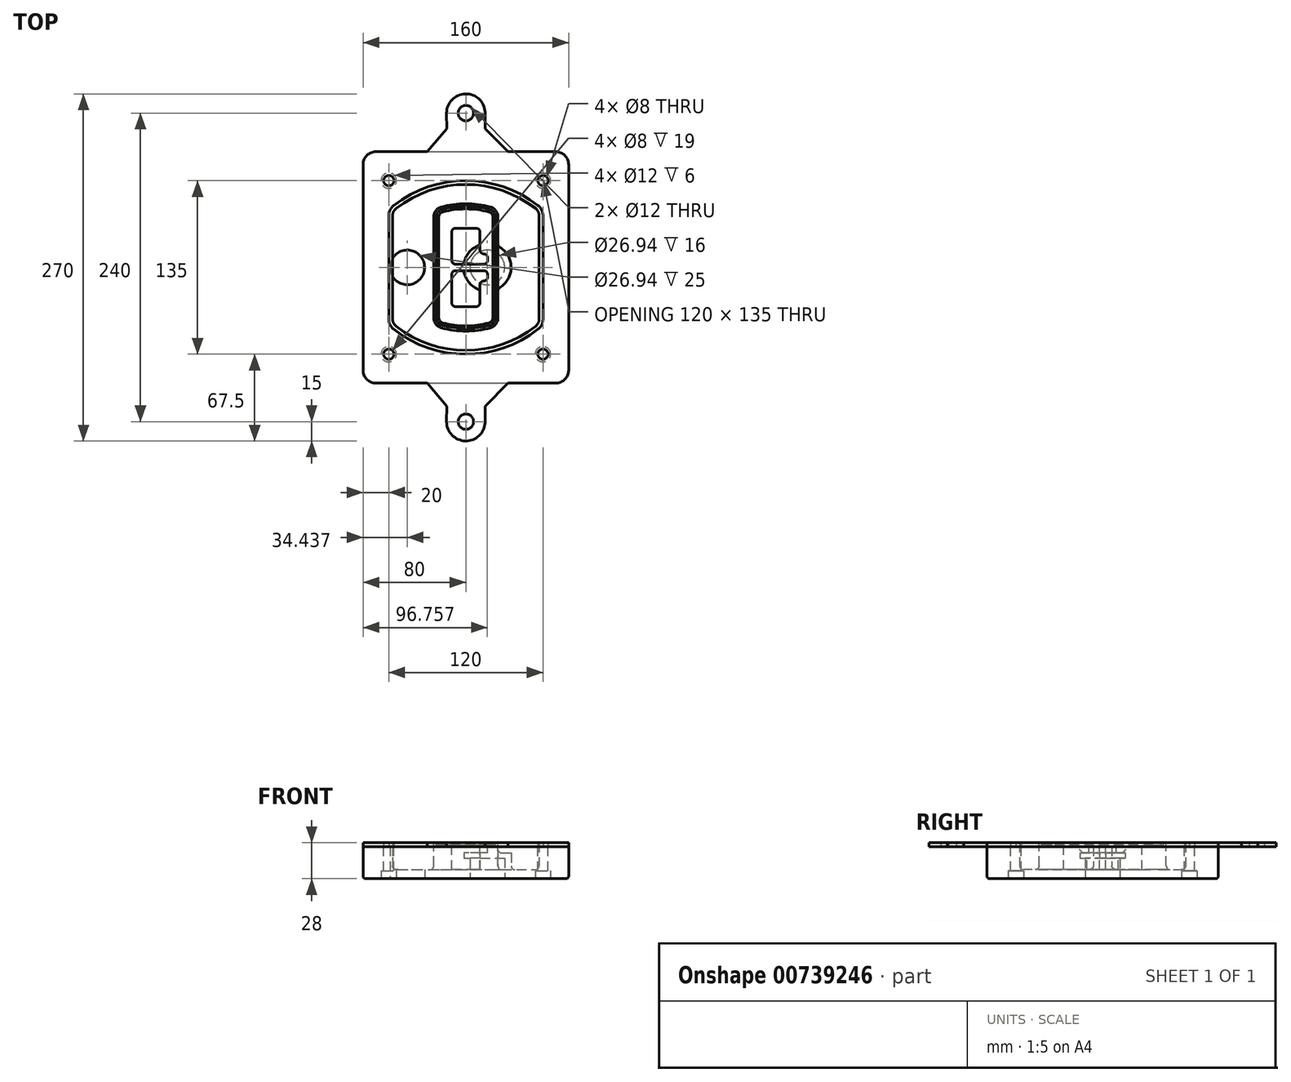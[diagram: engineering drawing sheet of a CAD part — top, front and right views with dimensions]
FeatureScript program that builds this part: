
annotation { "Feature Type Name" : "Feature", "Feature Type Description" : "" }
export const myFeature = defineFeature(function(context is Context, id is Id, definition is map)
    precondition{}
    {
        {
            var Q0;
            Q0=qCreatedBy(makeId("Top.planeOp"),FACE);
            var sketch = newSketch(context, id + "F0", { "sketchPlane" : qUnion([Q0])});
            skPoint(sketch, "E0.rect.middle", {"position": v(0, 0) * mm});
            skLineSegment(sketch, "E1.bottom", {"start": v(-70, -90) * mm, "end": v(70, -90) * mm});
            skLineSegment(sketch, "E1.top", {"start": v(-70, 90) * mm, "end": v(70, 90) * mm});
            skLineSegment(sketch, "E1.left", {"start": v(-80, -80) * mm, "end": v(-80, 80) * mm});
            skLineSegment(sketch, "E1.right", {"start": v(80, -80) * mm, "end": v(80, 80) * mm});
            skLineSegment(sketch, "E2", {"start": v(-80, 90) * mm, "end": v(80, -90) * mm, "construction": true});
            skLineSegment(sketch, "E3", {"start": v(80, 90) * mm, "end": v(-80, -90) * mm, "construction": true});
            skCircle(sketch, "E4", {"center": v(-60, 67.5) * mm, "radius": 4 * mm});
            skCircle(sketch, "E5", {"center": v(60, 67.5) * mm, "radius": 4 * mm});
            skCircle(sketch, "E6", {"center": v(60, -67.5) * mm, "radius": 4 * mm});
            skCircle(sketch, "E7", {"center": v(-60, -67.5) * mm, "radius": 4 * mm});
            skLineSegment(sketch, "E8", {"start": v(-60, 67.5) * mm, "end": v(60, 67.5) * mm, "construction": true});
            skLineSegment(sketch, "E9", {"start": v(60, 67.5) * mm, "end": v(60, -67.5) * mm, "construction": true});
            skLineSegment(sketch, "E10", {"start": v(60, -67.5) * mm, "end": v(-60, -67.5) * mm, "construction": true});
            skLineSegment(sketch, "E11", {"start": v(-60, -67.5) * mm, "end": v(-60, 67.5) * mm, "construction": true});
            skLineSegment(sketch, "E12", {"start": v(-60, 40.3) * mm, "end": v(-60, -40.3) * mm});
            skLineSegment(sketch, "E13", {"start": v(60, 40.3) * mm, "end": v(60, -40.3) * mm});
            skArc(sketch, "E14", {"start": v(56.15, 48.18) * mm, "mid": v(0, 67.5) * mm, "end": v(-56.15, 48.18) * mm});
            skArc(sketch, "E15", {"start": v(-56.15, -48.18) * mm, "mid": v(0, -67.5) * mm, "end": v(56.15, -48.18) * mm});
            skLineSegment(sketch, "E16", {"start": v(-60, 0) * mm, "end": v(60, 0) * mm, "construction": true});
            skPoint(sketch, "E17.visualSharp", {"position": v(-60, -45) * mm});
            skArc(sketch, "E17.filletArc", {"start": v(-60, -40.3) * mm, "mid": v(-58.99, -44.68) * mm, "end": v(-56.15, -48.18) * mm});
            skPoint(sketch, "E18.visualSharp", {"position": v(-60, 45) * mm});
            skArc(sketch, "E18.filletArc", {"start": v(-56.15, 48.18) * mm, "mid": v(-58.99, 44.68) * mm, "end": v(-60, 40.3) * mm});
            skPoint(sketch, "E19.visualSharp", {"position": v(60, 45) * mm});
            skArc(sketch, "E19.filletArc", {"start": v(60, 40.3) * mm, "mid": v(58.99, 44.68) * mm, "end": v(56.15, 48.18) * mm});
            skPoint(sketch, "E20.visualSharp", {"position": v(60, -45) * mm});
            skArc(sketch, "E20.filletArc", {"start": v(56.15, -48.18) * mm, "mid": v(58.99, -44.68) * mm, "end": v(60, -40.3) * mm});
            skPoint(sketch, "E21.visualSharp", {"position": v(-80, 90) * mm});
            skArc(sketch, "E21.filletArc", {"start": v(-70, 90) * mm, "mid": v(-77.07, 87.07) * mm, "end": v(-80, 80) * mm});
            skPoint(sketch, "E22.visualSharp", {"position": v(80, 90) * mm});
            skArc(sketch, "E22.filletArc", {"start": v(80, 80) * mm, "mid": v(77.07, 87.07) * mm, "end": v(70, 90) * mm});
            skPoint(sketch, "E23.visualSharp", {"position": v(80, -90) * mm});
            skArc(sketch, "E23.filletArc", {"start": v(70, -90) * mm, "mid": v(77.07, -87.07) * mm, "end": v(80, -80) * mm});
            skPoint(sketch, "E24.visualSharp", {"position": v(-80, -90) * mm});
            skArc(sketch, "E24.filletArc", {"start": v(-80, -80) * mm, "mid": v(-77.07, -87.07) * mm, "end": v(-70, -90) * mm});
            skArc(sketch, "E25.0", {"start": v(57, 40.3) * mm, "mid": v(56.3, 43.36) * mm, "end": v(54.3, 45.81) * mm});
            skLineSegment(sketch, "E25.1", {"start": v(57, 40.3) * mm, "end": v(57, -40.3) * mm});
            skArc(sketch, "E25.2", {"start": v(54.3, -45.81) * mm, "mid": v(56.3, -43.36) * mm, "end": v(57, -40.3) * mm});
            skArc(sketch, "E25.3", {"start": v(-54.3, -45.81) * mm, "mid": v(0, -64.5) * mm, "end": v(54.3, -45.81) * mm});
            skArc(sketch, "E25.4", {"start": v(-57, -40.3) * mm, "mid": v(-56.3, -43.36) * mm, "end": v(-54.3, -45.81) * mm});
            skArc(sketch, "E25.5", {"start": v(54.3, 45.81) * mm, "mid": v(0, 64.5) * mm, "end": v(-54.3, 45.81) * mm});
            skLineSegment(sketch, "E25.6", {"start": v(-57, 40.3) * mm, "end": v(-57, -40.3) * mm});
            skArc(sketch, "E25.7", {"start": v(-54.3, 45.81) * mm, "mid": v(-56.3, 43.36) * mm, "end": v(-57, 40.3) * mm});
            skArc(sketch, "E26.0", {"start": v(-58.62, 51.33) * mm, "mid": v(-62.58, 46.43) * mm, "end": v(-64, 40.3) * mm});
            skArc(sketch, "E26.1", {"start": v(58.62, 51.33) * mm, "mid": v(0, 71.5) * mm, "end": v(-58.62, 51.33) * mm});
            skArc(sketch, "E26.2", {"start": v(64, 40.3) * mm, "mid": v(62.58, 46.43) * mm, "end": v(58.62, 51.33) * mm});
            skLineSegment(sketch, "E26.3", {"start": v(64, 40.3) * mm, "end": v(64, -40.3) * mm});
            skArc(sketch, "E26.4", {"start": v(58.62, -51.33) * mm, "mid": v(62.58, -46.43) * mm, "end": v(64, -40.3) * mm});
            skLineSegment(sketch, "E26.5", {"start": v(-64, 40.3) * mm, "end": v(-64, -40.3) * mm});
            skArc(sketch, "E26.6", {"start": v(-58.62, -51.33) * mm, "mid": v(0, -71.5) * mm, "end": v(58.62, -51.33) * mm});
            skArc(sketch, "E26.7", {"start": v(-64, -40.3) * mm, "mid": v(-62.58, -46.43) * mm, "end": v(-58.62, -51.33) * mm});
            skSolve(sketch);
        }
        {
            var Q0;
            Q0=makeQuery(id+"F0.imprint","IMPRINT",FACE,{"disambiguationData":[TD([[makeQuery(id+"F0.imprint","IMPRINT",EDGE,{"derivedFrom":sQuery(id+"F0.wireOp",EDGE,"E1.bottom")}),1.0]])]});
            var Q1;
            Q1=makeQuery(id+"F0.imprint","IMPRINT",FACE,{"disambiguationData":[TD([[makeQuery(id+"F0.imprint","IMPRINT",EDGE,{"derivedFrom":sQuery(id+"F0.wireOp",EDGE,"E12")}),1.0]])]});
            var Q2;
            Q2=makeQuery(id+"F0.imprint","IMPRINT",FACE,{"disambiguationData":[TD([[makeQuery(id+"F0.imprint","IMPRINT",EDGE,{"derivedFrom":sQuery(id+"F0.wireOp",EDGE,"E25.0")}),1.0]])]});
            var Q3;
            Q3=makeQuery(id+"F0.imprint","IMPRINT",FACE,{"disambiguationData":[TD([[makeQuery(id+"F0.imprint","IMPRINT",EDGE,{"derivedFrom":sQuery(id+"F0.wireOp",EDGE,"E12")}),-1.0]])]});
            extrude(context, id + "F1", {"entities" : qUnion([Q0, Q1, Q2, Q3]), "oppositeDirection" : true, "depth" : 25 * mm});
        }
        {
            var Q0;
            Q0=makeQuery(id+"F0.imprint","IMPRINT",FACE,{"disambiguationData":[TD([[makeQuery(id+"F0.imprint","IMPRINT",EDGE,{"derivedFrom":sQuery(id+"F0.wireOp",EDGE,"E12")}),1.0]])]});
            extrude(context, id + "F2", {"entities" : qUnion([Q0]), "operationType" : NewBodyOperationType.ADD, "depth" : 3 * mm});
        }
        {
            var Q0;
            Q0=makeQuery(id+"F0.imprint","IMPRINT",FACE,{"disambiguationData":[TD([[makeQuery(id+"F0.imprint","IMPRINT",EDGE,{"derivedFrom":sQuery(id+"F0.wireOp",EDGE,"E25.0")}),1.0]])]});
            extrude(context, id + "F3", {"entities" : qUnion([Q0]), "operationType" : NewBodyOperationType.REMOVE, "oppositeDirection" : true, "depth" : 18 * mm});
        }
        {
            var Q0;
            Q0=makeQuery(id+"F2.opExtrude","CAP_FACE",FACE,{"disambiguationData":[OSD([sQuery(id+"F0.wireOp",EDGE,"E12"),sQuery(id+"F0.wireOp",EDGE,"E13"),sQuery(id+"F0.wireOp",EDGE,"E14"),sQuery(id+"F0.wireOp",EDGE,"E15"),sQuery(id+"F0.wireOp",EDGE,"E17.filletArc"),sQuery(id+"F0.wireOp",EDGE,"E18.filletArc"),sQuery(id+"F0.wireOp",EDGE,"E19.filletArc"),sQuery(id+"F0.wireOp",EDGE,"E20.filletArc"),sQuery(id+"F0.wireOp",EDGE,"E25.0"),sQuery(id+"F0.wireOp",EDGE,"E25.1"),sQuery(id+"F0.wireOp",EDGE,"E25.2"),sQuery(id+"F0.wireOp",EDGE,"E25.3"),sQuery(id+"F0.wireOp",EDGE,"E25.4"),sQuery(id+"F0.wireOp",EDGE,"E25.5"),sQuery(id+"F0.wireOp",EDGE,"E25.6"),sQuery(id+"F0.wireOp",EDGE,"E25.7")])],"isStart":false});
            var sketch = newSketch(context, id + "F4", { "sketchPlane" : qUnion([Q0])});
            skArc(sketch, "E27.0", {"start": v(-19.08, -46.97) * mm, "mid": v(0, -49.5) * mm, "end": v(19.08, -46.97) * mm});
            skArc(sketch, "E28.0", {"start": v(19.08, 46.97) * mm, "mid": v(0, 49.5) * mm, "end": v(-19.08, 46.97) * mm});
            skLineSegment(sketch, "E29", {"start": v(-25, 39.25) * mm, "end": v(-25, -39.25) * mm});
            skLineSegment(sketch, "E30", {"start": v(25, 39.25) * mm, "end": v(25, -39.25) * mm});
            skLineSegment(sketch, "E31", {"start": v(-25, 45.1) * mm, "end": v(25, 45.1) * mm, "construction": true});
            skLineSegment(sketch, "E32", {"start": v(-25, -45.1) * mm, "end": v(25, -45.1) * mm, "construction": true});
            skPoint(sketch, "E33.visualSharp", {"position": v(-25, 45.1) * mm});
            skArc(sketch, "E33.filletArc", {"start": v(-19.08, 46.97) * mm, "mid": v(-23.35, 44.11) * mm, "end": v(-25, 39.25) * mm});
            skPoint(sketch, "E34.visualSharp", {"position": v(25, 45.1) * mm});
            skArc(sketch, "E34.filletArc", {"start": v(25, 39.25) * mm, "mid": v(23.35, 44.11) * mm, "end": v(19.08, 46.97) * mm});
            skPoint(sketch, "E35.visualSharp", {"position": v(25, -45.1) * mm});
            skArc(sketch, "E35.filletArc", {"start": v(19.08, -46.97) * mm, "mid": v(23.35, -44.11) * mm, "end": v(25, -39.25) * mm});
            skPoint(sketch, "E36.visualSharp", {"position": v(-25, -45.1) * mm});
            skArc(sketch, "E36.filletArc", {"start": v(-25, -39.25) * mm, "mid": v(-23.35, -44.11) * mm, "end": v(-19.08, -46.97) * mm});
            skArc(sketch, "E37.0", {"start": v(54.3, 45.81) * mm, "mid": v(0, 64.5) * mm, "end": v(-54.3, 45.81) * mm});
            skArc(sketch, "E37.1", {"start": v(-54.3, 45.81) * mm, "mid": v(-56.3, 43.36) * mm, "end": v(-57, 40.3) * mm});
            skLineSegment(sketch, "E37.2", {"start": v(-57, 40.3) * mm, "end": v(-57, -40.3) * mm});
            skArc(sketch, "E37.3", {"start": v(-57, -40.3) * mm, "mid": v(-56.3, -43.36) * mm, "end": v(-54.3, -45.81) * mm});
            skArc(sketch, "E37.4", {"start": v(-54.3, -45.81) * mm, "mid": v(0, -64.5) * mm, "end": v(54.3, -45.81) * mm});
            skArc(sketch, "E37.5", {"start": v(54.3, -45.81) * mm, "mid": v(56.3, -43.36) * mm, "end": v(57, -40.3) * mm});
            skLineSegment(sketch, "E37.6", {"start": v(57, 40.3) * mm, "end": v(57, -40.3) * mm});
            skArc(sketch, "E37.7", {"start": v(57, 40.3) * mm, "mid": v(56.3, 43.36) * mm, "end": v(54.3, 45.81) * mm});
            skLineSegment(sketch, "E38.0", {"start": v(23, 39.25) * mm, "end": v(23, -39.25) * mm});
            skArc(sketch, "E38.1", {"start": v(18.56, -45.04) * mm, "mid": v(21.76, -42.9) * mm, "end": v(23, -39.25) * mm});
            skArc(sketch, "E38.2", {"start": v(-18.56, -45.04) * mm, "mid": v(0, -47.5) * mm, "end": v(18.56, -45.04) * mm});
            skArc(sketch, "E38.3", {"start": v(-23, -39.25) * mm, "mid": v(-21.76, -42.9) * mm, "end": v(-18.56, -45.04) * mm});
            skLineSegment(sketch, "E38.4", {"start": v(-23, 39.25) * mm, "end": v(-23, -39.25) * mm});
            skArc(sketch, "E38.5", {"start": v(23, 39.25) * mm, "mid": v(21.76, 42.9) * mm, "end": v(18.56, 45.04) * mm});
            skArc(sketch, "E38.6", {"start": v(-18.56, 45.04) * mm, "mid": v(-21.76, 42.9) * mm, "end": v(-23, 39.25) * mm});
            skArc(sketch, "E38.7", {"start": v(18.56, 45.04) * mm, "mid": v(0, 47.5) * mm, "end": v(-18.56, 45.04) * mm});
            skArc(sketch, "E39.0", {"start": v(21, 39.25) * mm, "mid": v(20.18, 41.68) * mm, "end": v(18.04, 43.1) * mm});
            skLineSegment(sketch, "E39.1", {"start": v(21, 39.25) * mm, "end": v(21, -39.25) * mm});
            skArc(sketch, "E39.2", {"start": v(18.04, -43.1) * mm, "mid": v(20.18, -41.68) * mm, "end": v(21, -39.25) * mm});
            skArc(sketch, "E39.3", {"start": v(-18.04, -43.1) * mm, "mid": v(0, -45.5) * mm, "end": v(18.04, -43.1) * mm});
            skArc(sketch, "E39.4", {"start": v(-21, -39.25) * mm, "mid": v(-20.18, -41.68) * mm, "end": v(-18.04, -43.1) * mm});
            skArc(sketch, "E39.5", {"start": v(18.04, 43.1) * mm, "mid": v(0, 45.5) * mm, "end": v(-18.04, 43.1) * mm});
            skLineSegment(sketch, "E39.6", {"start": v(-21, 39.25) * mm, "end": v(-21, -39.25) * mm});
            skArc(sketch, "E39.7", {"start": v(-18.04, 43.1) * mm, "mid": v(-20.18, 41.68) * mm, "end": v(-21, 39.25) * mm});
            skLineSegment(sketch, "E40", {"start": v(-25, 0) * mm, "end": v(25, 0) * mm, "construction": true});
            skLineSegment(sketch, "E41", {"start": v(-11, 5.5) * mm, "end": v(-11, 27.5) * mm});
            skLineSegment(sketch, "E42", {"start": v(-8, 30.5) * mm, "end": v(8, 30.5) * mm});
            skLineSegment(sketch, "E43", {"start": v(11, 27.5) * mm, "end": v(11, 13.5) * mm});
            skLineSegment(sketch, "E44", {"start": v(14, 10.5) * mm, "end": v(14, 10.5) * mm});
            skLineSegment(sketch, "E45", {"start": v(17, 7.5) * mm, "end": v(17, 5.5) * mm});
            skLineSegment(sketch, "E46", {"start": v(14, 2.5) * mm, "end": v(-8, 2.5) * mm});
            skPoint(sketch, "E47.visualSharp", {"position": v(-11, 30.5) * mm});
            skArc(sketch, "E47.filletArc", {"start": v(-8, 30.5) * mm, "mid": v(-10.12, 29.62) * mm, "end": v(-11, 27.5) * mm});
            skPoint(sketch, "E48.visualSharp", {"position": v(11, 30.5) * mm});
            skArc(sketch, "E48.filletArc", {"start": v(11, 27.5) * mm, "mid": v(10.12, 29.62) * mm, "end": v(8, 30.5) * mm});
            skPoint(sketch, "E49.visualSharp", {"position": v(11, 10.5) * mm});
            skArc(sketch, "E49.filletArc", {"start": v(11, 13.5) * mm, "mid": v(11.88, 11.38) * mm, "end": v(14, 10.5) * mm});
            skPoint(sketch, "E50.visualSharp", {"position": v(17, 10.5) * mm});
            skArc(sketch, "E50.filletArc", {"start": v(17, 7.5) * mm, "mid": v(16.12, 9.62) * mm, "end": v(14, 10.5) * mm});
            skPoint(sketch, "E51.visualSharp", {"position": v(17, 2.5) * mm});
            skArc(sketch, "E51.filletArc", {"start": v(14, 2.5) * mm, "mid": v(16.12, 3.38) * mm, "end": v(17, 5.5) * mm});
            skPoint(sketch, "E52.visualSharp", {"position": v(-11, 2.5) * mm});
            skArc(sketch, "E52.filletArc", {"start": v(-11, 5.5) * mm, "mid": v(-10.12, 3.38) * mm, "end": v(-8, 2.5) * mm});
            skLineSegment(sketch, "E53.0.MirrorCS", {"start": v(14, -2.5) * mm, "end": v(-8, -2.5) * mm});
            skArc(sketch, "E54.0.MirrorCS", {"start": v(-11, -5.5) * mm, "mid": v(-10.12, -3.38) * mm, "end": v(-8, -2.5) * mm});
            skLineSegment(sketch, "E55.0.MirrorCS", {"start": v(-11, -5.5) * mm, "end": v(-11, -27.5) * mm});
            skArc(sketch, "E56.0.MirrorCS", {"start": v(-8, -30.5) * mm, "mid": v(-10.12, -29.62) * mm, "end": v(-11, -27.5) * mm});
            skLineSegment(sketch, "E57.0.MirrorCS", {"start": v(-8, -30.5) * mm, "end": v(8, -30.5) * mm});
            skArc(sketch, "E58.0.MirrorCS", {"start": v(11, -27.5) * mm, "mid": v(10.12, -29.62) * mm, "end": v(8, -30.5) * mm});
            skLineSegment(sketch, "E59.0.MirrorCS", {"start": v(11, -27.5) * mm, "end": v(11, -13.5) * mm});
            skArc(sketch, "E60.0.MirrorCS", {"start": v(11, -13.5) * mm, "mid": v(11.88, -11.38) * mm, "end": v(14, -10.5) * mm});
            skArc(sketch, "E61.0.MirrorCS", {"start": v(17, -7.5) * mm, "mid": v(16.12, -9.62) * mm, "end": v(14, -10.5) * mm});
            skLineSegment(sketch, "E62.0.MirrorCS", {"start": v(17, -7.5) * mm, "end": v(17, -5.5) * mm});
            skArc(sketch, "E63.0.MirrorCS", {"start": v(14, -2.5) * mm, "mid": v(16.12, -3.38) * mm, "end": v(17, -5.5) * mm});
            skSolve(sketch);
        }
        {
            var Q0;
            Q0=makeQuery(id+"F4.imprint","IMPRINT",FACE,{"disambiguationData":[TD([[makeQuery(id+"F4.imprint","IMPRINT",EDGE,{"derivedFrom":sQuery(id+"F4.wireOp",EDGE,"E27.0")}),1.0]])]});
            var Q1;
            Q1=makeQuery(id+"F4.imprint","IMPRINT",FACE,{"disambiguationData":[TD([[makeQuery(id+"F4.imprint","IMPRINT",EDGE,{"derivedFrom":sQuery(id+"F4.wireOp",EDGE,"E38.0")}),-1.0]])]});
            var Q2;
            Q2=makeQuery(id+"F4.imprint","IMPRINT",FACE,{"disambiguationData":[TD([[makeQuery(id+"F4.imprint","IMPRINT",EDGE,{"derivedFrom":sQuery(id+"F4.wireOp",EDGE,"E39.0")}),1.0]])]});
            extrude(context, id + "F5", {"entities" : qUnion([Q0, Q1, Q2]), "operationType" : NewBodyOperationType.ADD, "endBound" : BoundingType.UP_TO_NEXT, "oppositeDirection" : true, "depth" : 25 * mm});
        }
        {
            var Q0;
            Q0=makeQuery(id+"F4.imprint","IMPRINT",FACE,{"disambiguationData":[TD([[makeQuery(id+"F4.imprint","IMPRINT",EDGE,{"derivedFrom":sQuery(id+"F4.wireOp",EDGE,"E38.0")}),-1.0]])]});
            extrude(context, id + "F6", {"entities" : qUnion([Q0]), "operationType" : NewBodyOperationType.REMOVE, "oppositeDirection" : true, "depth" : 2 * mm});
        }
        {
            var Q0;
            Q0=makeQuery(id+"F1.opExtrude","CAP_FACE",FACE,{"disambiguationData":[OSD([sQuery(id+"F0.wireOp",EDGE,"E1.bottom"),sQuery(id+"F0.wireOp",EDGE,"E1.top"),sQuery(id+"F0.wireOp",EDGE,"E1.left"),sQuery(id+"F0.wireOp",EDGE,"E1.right"),sQuery(id+"F0.wireOp",EDGE,"E4"),sQuery(id+"F0.wireOp",EDGE,"E5"),sQuery(id+"F0.wireOp",EDGE,"E6"),sQuery(id+"F0.wireOp",EDGE,"E7"),sQuery(id+"F0.wireOp",EDGE,"E21.filletArc"),sQuery(id+"F0.wireOp",EDGE,"E22.filletArc"),sQuery(id+"F0.wireOp",EDGE,"E23.filletArc"),sQuery(id+"F0.wireOp",EDGE,"E24.filletArc")])],"isStart":false});
            var sketch = newSketch(context, id + "F7", { "sketchPlane" : qUnion([Q0])});
            skCircle(sketch, "E64", {"center": v(16.76, 0) * mm, "radius": 13.47 * mm});
            skCircle(sketch, "E65", {"center": v(-45.56, 0) * mm, "radius": 13.47 * mm});
            skLineSegment(sketch, "E66", {"start": v(80, 0) * mm, "end": v(-80, 0) * mm});
            skCircle(sketch, "E67", {"center": v(16.76, 0) * mm, "radius": 18.47 * mm});
            skCircle(sketch, "E68", {"center": v(60, -67.5) * mm, "radius": 6 * mm});
            skCircle(sketch, "E69", {"center": v(-60, -67.5) * mm, "radius": 6 * mm});
            skCircle(sketch, "E70", {"center": v(-60, 67.5) * mm, "radius": 6 * mm});
            skCircle(sketch, "E71", {"center": v(60, 67.5) * mm, "radius": 6 * mm});
            skSolve(sketch);
        }
        {
            var Q0;
            {var subQ1=sQuery(id+"F7.wireOp",EDGE,"E66");var subQ4=sQuery(id+"F7.wireOp",EDGE,"E64");var subQ6=makeQuery(id+"F7.imprint","INTERSECT",VERTEX,{"disambiguationData":[OD(0.0)],"derivedFrom":[subQ4,subQ1]});Q0=makeQuery(id+"F7.imprint","IMPRINT",FACE,{"disambiguationData":[TD([[makeQuery(id+"F7.imprint","IMPRINT",EDGE,{"disambiguationData":[TD([[subQ6,-1.0]])],"derivedFrom":subQ4}),-1.0]])]});}
            var Q1;
            {var subQ0=sQuery(id+"F7.wireOp",EDGE,"E66");var subQ1=sQuery(id+"F7.wireOp",EDGE,"E64");var subQ3=makeQuery(id+"F7.imprint","INTERSECT",VERTEX,{"disambiguationData":[OD(0.0)],"derivedFrom":[subQ1,subQ0]});Q1=makeQuery(id+"F7.imprint","IMPRINT",FACE,{"disambiguationData":[TD([[makeQuery(id+"F7.imprint","IMPRINT",EDGE,{"disambiguationData":[TD([[subQ3,-1.0]])],"derivedFrom":subQ1}),1.0]])]});}
            var Q2;
            {var subQ0=sQuery(id+"F7.wireOp",EDGE,"E66");var subQ1=sQuery(id+"F7.wireOp",EDGE,"E64");var subQ3=makeQuery(id+"F7.imprint","INTERSECT",VERTEX,{"disambiguationData":[OD(0.0)],"derivedFrom":[subQ1,subQ0]});Q2=makeQuery(id+"F7.imprint","IMPRINT",FACE,{"disambiguationData":[TD([[makeQuery(id+"F7.imprint","IMPRINT",EDGE,{"disambiguationData":[TD([[subQ3,1.0]])],"derivedFrom":subQ1}),1.0]])]});}
            var Q3;
            {var subQ1=sQuery(id+"F7.wireOp",EDGE,"E66");var subQ4=sQuery(id+"F7.wireOp",EDGE,"E64");var subQ6=makeQuery(id+"F7.imprint","INTERSECT",VERTEX,{"disambiguationData":[OD(0.0)],"derivedFrom":[subQ4,subQ1]});Q3=makeQuery(id+"F7.imprint","IMPRINT",FACE,{"disambiguationData":[TD([[makeQuery(id+"F7.imprint","IMPRINT",EDGE,{"disambiguationData":[TD([[subQ6,1.0]])],"derivedFrom":subQ4}),-1.0]])]});}
            extrude(context, id + "F8", {"entities" : qUnion([Q0, Q1, Q2, Q3]), "operationType" : NewBodyOperationType.ADD, "oppositeDirection" : true, "depth" : 20 * mm});
        }
        {
            var Q0;
            {var subQ0=sQuery(id+"F7.wireOp",EDGE,"E66");var subQ1=sQuery(id+"F7.wireOp",EDGE,"E64");var subQ3=makeQuery(id+"F7.imprint","INTERSECT",VERTEX,{"disambiguationData":[OD(0.0)],"derivedFrom":[subQ1,subQ0]});Q0=makeQuery(id+"F7.imprint","IMPRINT",FACE,{"disambiguationData":[TD([[makeQuery(id+"F7.imprint","IMPRINT",EDGE,{"disambiguationData":[TD([[subQ3,-1.0]])],"derivedFrom":subQ1}),1.0]])]});}
            var Q1;
            {var subQ0=sQuery(id+"F7.wireOp",EDGE,"E66");var subQ1=sQuery(id+"F7.wireOp",EDGE,"E64");var subQ3=makeQuery(id+"F7.imprint","INTERSECT",VERTEX,{"disambiguationData":[OD(0.0)],"derivedFrom":[subQ1,subQ0]});Q1=makeQuery(id+"F7.imprint","IMPRINT",FACE,{"disambiguationData":[TD([[makeQuery(id+"F7.imprint","IMPRINT",EDGE,{"disambiguationData":[TD([[subQ3,1.0]])],"derivedFrom":subQ1}),1.0]])]});}
            extrude(context, id + "F9", {"entities" : qUnion([Q0, Q1]), "operationType" : NewBodyOperationType.REMOVE, "oppositeDirection" : true, "depth" : 16 * mm});
        }
        {
            var Q0;
            {var subQ0=sQuery(id+"F7.wireOp",EDGE,"E66");var subQ1=sQuery(id+"F7.wireOp",EDGE,"E65");var subQ3=makeQuery(id+"F7.imprint","INTERSECT",VERTEX,{"disambiguationData":[OD(0.0)],"derivedFrom":[subQ1,subQ0]});Q0=makeQuery(id+"F7.imprint","IMPRINT",FACE,{"disambiguationData":[TD([[makeQuery(id+"F7.imprint","IMPRINT",EDGE,{"disambiguationData":[TD([[subQ3,-1.0]])],"derivedFrom":subQ1}),1.0]])]});}
            var Q1;
            {var subQ0=sQuery(id+"F7.wireOp",EDGE,"E66");var subQ1=sQuery(id+"F7.wireOp",EDGE,"E65");var subQ3=makeQuery(id+"F7.imprint","INTERSECT",VERTEX,{"disambiguationData":[OD(0.0)],"derivedFrom":[subQ1,subQ0]});Q1=makeQuery(id+"F7.imprint","IMPRINT",FACE,{"disambiguationData":[TD([[makeQuery(id+"F7.imprint","IMPRINT",EDGE,{"disambiguationData":[TD([[subQ3,1.0]])],"derivedFrom":subQ1}),1.0]])]});}
            extrude(context, id + "F10", {"entities" : qUnion([Q0, Q1]), "operationType" : NewBodyOperationType.REMOVE, "oppositeDirection" : true, "depth" : 25 * mm});
        }
        {
            var Q0;
            Q0=makeQuery(id+"F7.imprint","IMPRINT",FACE,{"disambiguationData":[TD([[makeQuery(id+"F7.imprint","IMPRINT",EDGE,{"derivedFrom":sQuery(id+"F7.wireOp",EDGE,"E68")}),1.0]])]});
            var Q1;
            Q1=makeQuery(id+"F7.imprint","IMPRINT",FACE,{"disambiguationData":[TD([[makeQuery(id+"F7.imprint","IMPRINT",EDGE,{"derivedFrom":makeQuery(id+"F1.opExtrude","CAP_EDGE",EDGE,{"disambiguationData":[OSD([sQuery(id+"F0.wireOp",EDGE,"E5")])],"isStart":false})}),-1.0]])]});
            var Q2;
            Q2=makeQuery(id+"F7.imprint","IMPRINT",FACE,{"disambiguationData":[TD([[makeQuery(id+"F7.imprint","IMPRINT",EDGE,{"derivedFrom":sQuery(id+"F7.wireOp",EDGE,"E69")}),1.0]])]});
            var Q3;
            Q3=makeQuery(id+"F7.imprint","IMPRINT",FACE,{"disambiguationData":[TD([[makeQuery(id+"F7.imprint","IMPRINT",EDGE,{"derivedFrom":makeQuery(id+"F1.opExtrude","CAP_EDGE",EDGE,{"disambiguationData":[OSD([sQuery(id+"F0.wireOp",EDGE,"E4")])],"isStart":false})}),-1.0]])]});
            var Q4;
            Q4=makeQuery(id+"F7.imprint","IMPRINT",FACE,{"disambiguationData":[TD([[makeQuery(id+"F7.imprint","IMPRINT",EDGE,{"derivedFrom":sQuery(id+"F7.wireOp",EDGE,"E70")}),1.0]])]});
            var Q5;
            Q5=makeQuery(id+"F7.imprint","IMPRINT",FACE,{"disambiguationData":[TD([[makeQuery(id+"F7.imprint","IMPRINT",EDGE,{"derivedFrom":makeQuery(id+"F1.opExtrude","CAP_EDGE",EDGE,{"disambiguationData":[OSD([sQuery(id+"F0.wireOp",EDGE,"E7")])],"isStart":false})}),-1.0]])]});
            var Q6;
            Q6=makeQuery(id+"F7.imprint","IMPRINT",FACE,{"disambiguationData":[TD([[makeQuery(id+"F7.imprint","IMPRINT",EDGE,{"derivedFrom":sQuery(id+"F7.wireOp",EDGE,"E71")}),1.0]])]});
            var Q7;
            Q7=makeQuery(id+"F7.imprint","IMPRINT",FACE,{"disambiguationData":[TD([[makeQuery(id+"F7.imprint","IMPRINT",EDGE,{"derivedFrom":makeQuery(id+"F1.opExtrude","CAP_EDGE",EDGE,{"disambiguationData":[OSD([sQuery(id+"F0.wireOp",EDGE,"E6")])],"isStart":false})}),-1.0]])]});
            extrude(context, id + "F11", {"entities" : qUnion([Q0, Q1, Q2, Q3, Q4, Q5, Q6, Q7]), "operationType" : NewBodyOperationType.REMOVE, "oppositeDirection" : true, "depth" : 6 * mm});
        }
        {
            var Q0;
            Q0=makeQuery(id+"F9.boolean.opBoolean","COPY",FACE,{"derivedFrom":makeQuery(id+"F9.opExtrude","CAP_FACE",FACE,{"disambiguationData":[OSD([sQuery(id+"F7.wireOp",EDGE,"E64")])],"isStart":false})});
            var sketch = newSketch(context, id + "F12", { "sketchPlane" : qUnion([Q0])});
            skArc(sketch, "E72.0", {"start": v(11, 17.55) * mm, "mid": v(2.57, 11.82) * mm, "end": v(-1.54, 2.5) * mm});
            skArc(sketch, "E72.1", {"start": v(-1.54, -2.5) * mm, "mid": v(2.57, -11.82) * mm, "end": v(11, -17.55) * mm});
            skLineSegment(sketch, "E73", {"start": v(-1.54, -2.5) * mm, "end": v(14, -2.5) * mm});
            skLineSegment(sketch, "E74.0", {"start": v(14, 2.5) * mm, "end": v(-1.54, 2.5) * mm});
            skArc(sketch, "E74.1", {"start": v(14, 2.5) * mm, "mid": v(16.12, 3.38) * mm, "end": v(17, 5.5) * mm});
            skLineSegment(sketch, "E74.2", {"start": v(17, 7.5) * mm, "end": v(17, 5.5) * mm});
            skArc(sketch, "E74.3", {"start": v(17, 7.5) * mm, "mid": v(16.12, 9.62) * mm, "end": v(14, 10.5) * mm});
            skArc(sketch, "E74.4", {"start": v(11, 13.5) * mm, "mid": v(11.88, 11.38) * mm, "end": v(14, 10.5) * mm});
            skLineSegment(sketch, "E74.5", {"start": v(11, 17.55) * mm, "end": v(11, 13.5) * mm});
            skLineSegment(sketch, "E74.7", {"start": v(14, -2.5) * mm, "end": v(-1.54, -2.5) * mm});
            skArc(sketch, "E74.8", {"start": v(14, -2.5) * mm, "mid": v(16.12, -3.38) * mm, "end": v(17, -5.5) * mm});
            skLineSegment(sketch, "E74.9", {"start": v(17, -7.5) * mm, "end": v(17, -5.5) * mm});
            skArc(sketch, "E74.10", {"start": v(17, -7.5) * mm, "mid": v(16.12, -9.62) * mm, "end": v(14, -10.5) * mm});
            skArc(sketch, "E74.11", {"start": v(11, -13.5) * mm, "mid": v(11.88, -11.38) * mm, "end": v(14, -10.5) * mm});
            skLineSegment(sketch, "E74.12", {"start": v(11, -17.55) * mm, "end": v(11, -13.5) * mm});
            skPoint(sketch, "E75.orphan", {"position": v(11, -27.5) * mm});
            skPoint(sketch, "E76.orphan", {"position": v(-8, -2.5) * mm});
            skPoint(sketch, "E77.orphan", {"position": v(-8, 2.5) * mm});
            skPoint(sketch, "E78.orphan", {"position": v(11, 27.5) * mm});
            skSolve(sketch);
        }
        {
            var Q0;
            {var subQ7=sQuery(id+"F12.wireOp",EDGE,"E72.0");var subQ14=sQuery(id+"F12.wireOp",EDGE,"E72.1");var subQ16=sQuery(id+"F12.wireOp",EDGE,"E74.1");var subQ18=sQuery(id+"F12.wireOp",EDGE,"E74.8");Q0=qUnion([makeQuery(id+"F12.imprint","IMPRINT",FACE,{"disambiguationData":[TD([[makeQuery(id+"F12.imprint","IMPRINT",EDGE,{"derivedFrom":subQ7}),1.0]])]}),makeQuery(id+"F12.imprint","IMPRINT",FACE,{"disambiguationData":[TD([[makeQuery(id+"F12.imprint","IMPRINT",EDGE,{"derivedFrom":subQ14}),1.0]])]}),makeQuery(id+"F12.imprint","IMPRINT",FACE,{"disambiguationData":[TD([[makeQuery(id+"F12.imprint","IMPRINT",EDGE,{"derivedFrom":subQ16}),1.0]])]}),makeQuery(id+"F12.imprint","IMPRINT",FACE,{"disambiguationData":[TD([[makeQuery(id+"F12.imprint","IMPRINT",EDGE,{"derivedFrom":subQ18}),-1.0]])]})]);}
            var Q1;
            Q1=makeQuery(id+"F5.boolean.opBoolean","SPLIT",FACE,{"disambiguationData":[TD([makeQuery(id+"F5.opExtrude","SWEPT_FACE",FACE,{"disambiguationData":[OSD([sQuery(id+"F4.wireOp",EDGE,"E41")])]})])],"derivedFrom":makeQuery(id+"F3.boolean.opBoolean","COPY",FACE,{"derivedFrom":makeQuery(id+"F3.opExtrude","CAP_FACE",FACE,{"disambiguationData":[OSD([sQuery(id+"F0.wireOp",EDGE,"E25.0"),sQuery(id+"F0.wireOp",EDGE,"E25.1"),sQuery(id+"F0.wireOp",EDGE,"E25.2"),sQuery(id+"F0.wireOp",EDGE,"E25.3"),sQuery(id+"F0.wireOp",EDGE,"E25.4"),sQuery(id+"F0.wireOp",EDGE,"E25.5"),sQuery(id+"F0.wireOp",EDGE,"E25.6"),sQuery(id+"F0.wireOp",EDGE,"E25.7")])],"isStart":false})})});
            extrude(context, id + "F13", {"entities" : qUnion([Q0]), "operationType" : NewBodyOperationType.REMOVE, "endBound" : BoundingType.UP_TO_SURFACE, "endBoundEntityFace" : qUnion([Q1]), "depth" : 25 * mm});
        }
        {
            var Q0;
            Q0=makeQuery(id+"F3.boolean.opBoolean","COPY",EDGE,{"derivedFrom":makeQuery(id+"F3.opExtrude","CAP_EDGE",EDGE,{"disambiguationData":[OSD([sQuery(id+"F0.wireOp",EDGE,"E25.6")])],"isStart":false})});
            var Q1;
            Q1=makeQuery(id+"F8.boolean.opBoolean","INTERSECT",EDGE,{"derivedFrom":[makeQuery(id+"F5.opExtrude","SWEPT_FACE",FACE,{"disambiguationData":[OSD([sQuery(id+"F4.wireOp",EDGE,"E30")])]}),makeQuery(id+"F8.opExtrude","CAP_FACE",FACE,{"disambiguationData":[OSD([sQuery(id+"F7.wireOp",EDGE,"E67")])],"isStart":false})]});
            var Q2;
            Q2=makeQuery(id+"F8.boolean.opBoolean","INTERSECT",EDGE,{"disambiguationData":[OD(1.0)],"derivedFrom":[makeQuery(id+"F5.opExtrude","SWEPT_FACE",FACE,{"disambiguationData":[OSD([sQuery(id+"F4.wireOp",EDGE,"E30")])]}),makeQuery(id+"F8.opExtrude","SWEPT_FACE",FACE,{"disambiguationData":[OSD([sQuery(id+"F7.wireOp",EDGE,"E67")])]})]});
            var Q3;
            {var subQ0=sQuery(id+"F4.wireOp",EDGE,"E30");Q3=makeQuery(id+"F8.boolean.opBoolean","SPLIT",EDGE,{"disambiguationData":[TD([makeQuery(id+"F5.opExtrude","SWEPT_FACE",FACE,{"disambiguationData":[OSD([sQuery(id+"F4.wireOp",EDGE,"E35.filletArc")])]})])],"derivedFrom":makeQuery(id+"F5.opExtrude","CAP_EDGE",EDGE,{"disambiguationData":[OSD([subQ0])],"isStart":false})});}
            var Q4;
            {var subQ0=sQuery(id+"F0.wireOp",EDGE,"E25.7");var subQ1=sQuery(id+"F0.wireOp",EDGE,"E25.1");var subQ2=sQuery(id+"F0.wireOp",EDGE,"E25.6");var subQ3=sQuery(id+"F0.wireOp",EDGE,"E25.5");var subQ4=sQuery(id+"F0.wireOp",EDGE,"E25.4");var subQ5=sQuery(id+"F0.wireOp",EDGE,"E25.0");var subQ6=sQuery(id+"F0.wireOp",EDGE,"E25.2");var subQ7=sQuery(id+"F0.wireOp",EDGE,"E25.3");Q4=makeQuery(id+"F8.boolean.opBoolean","INTERSECT",EDGE,{"derivedFrom":[makeQuery(id+"F5.boolean.opBoolean","SPLIT",FACE,{"disambiguationData":[TD([makeQuery(id+"F2.opExtrude","SWEPT_FACE",FACE,{"disambiguationData":[OSD([subQ5])]})])],"derivedFrom":makeQuery(id+"F3.boolean.opBoolean","COPY",FACE,{"derivedFrom":makeQuery(id+"F3.opExtrude","CAP_FACE",FACE,{"disambiguationData":[OSD([subQ5,subQ1,subQ6,subQ7,subQ4,subQ3,subQ2,subQ0])],"isStart":false})})}),makeQuery(id+"F8.opExtrude","SWEPT_FACE",FACE,{"disambiguationData":[OSD([sQuery(id+"F7.wireOp",EDGE,"E67")])]})]});}
            var Q5;
            Q5=makeQuery(id+"F8.boolean.opBoolean","INTERSECT",EDGE,{"disambiguationData":[OD(0.0)],"derivedFrom":[makeQuery(id+"F5.opExtrude","SWEPT_FACE",FACE,{"disambiguationData":[OSD([sQuery(id+"F4.wireOp",EDGE,"E30")])]}),makeQuery(id+"F8.opExtrude","SWEPT_FACE",FACE,{"disambiguationData":[OSD([sQuery(id+"F7.wireOp",EDGE,"E67")])]})]});
            fillet(context, id + "F14", {"entities" : qUnion([Q0, Q1, Q2, Q3, Q4, Q5]), "radius" : 3 * mm, "tangentPropagation" : true, "allowEdgeOverflow" : false});
        }
        {
            var Q0;
            Q0=makeQuery(id+"F1.opExtrude","CAP_EDGE",EDGE,{"disambiguationData":[OSD([sQuery(id+"F0.wireOp",EDGE,"E1.bottom")])],"isStart":false});
            fillet(context, id + "F15", {"entities" : qUnion([Q0]), "radius" : 2 * mm, "tangentPropagation" : true, "allowEdgeOverflow" : false});
        }
        {
            var Q0;
            {var subQ0=sQuery(id+"F0.wireOp",EDGE,"E21.filletArc");var subQ1=sQuery(id+"F0.wireOp",EDGE,"E7");var subQ2=sQuery(id+"F0.wireOp",EDGE,"E6");var subQ3=sQuery(id+"F0.wireOp",EDGE,"E5");var subQ4=sQuery(id+"F0.wireOp",EDGE,"E4");var subQ5=sQuery(id+"F0.wireOp",EDGE,"E22.filletArc");var subQ6=sQuery(id+"F0.wireOp",EDGE,"E1.bottom");var subQ7=sQuery(id+"F0.wireOp",EDGE,"E1.right");var subQ8=sQuery(id+"F0.wireOp",EDGE,"E1.top");var subQ9=sQuery(id+"F0.wireOp",EDGE,"E1.left");var subQ10=sQuery(id+"F0.wireOp",EDGE,"E23.filletArc");var subQ11=sQuery(id+"F0.wireOp",EDGE,"E24.filletArc");Q0=makeQuery(id+"F2.boolean.opBoolean","SPLIT",FACE,{"disambiguationData":[TD([makeQuery(id+"F1.opExtrude","SWEPT_FACE",FACE,{"disambiguationData":[OSD([subQ6])]})])],"derivedFrom":makeQuery(id+"F1.opExtrude","CAP_FACE",FACE,{"disambiguationData":[OSD([subQ6,subQ8,subQ9,subQ7,subQ4,subQ3,subQ2,subQ1,subQ0,subQ5,subQ10,subQ11])],"isStart":true})});}
            var sketch = newSketch(context, id + "F16", { "sketchPlane" : qUnion([Q0])});
            skLineSegment(sketch, "E79", {"start": v(0, 90) * mm, "end": v(0, 120) * mm, "construction": true});
            skCircle(sketch, "E80", {"center": v(0, 120) * mm, "radius": 6 * mm});
            skLineSegment(sketch, "E81", {"start": v(-30.05, 90) * mm, "end": v(-14.87, 108) * mm});
            skLineSegment(sketch, "E82", {"start": v(32.98, 90) * mm, "end": v(14.98, 108) * mm});
            skLineSegment(sketch, "E83", {"start": v(-14.87, 108) * mm, "end": v(-15, 120) * mm});
            skLineSegment(sketch, "E84", {"start": v(14.98, 108) * mm, "end": v(14.98, 120.77) * mm});
            skArc(sketch, "E85", {"start": v(14.98, 120.77) * mm, "mid": v(-0.39, 135) * mm, "end": v(-15, 120) * mm});
            skLineSegment(sketch, "E86", {"start": v(-80, 0) * mm, "end": v(80, 0) * mm, "construction": true});
            skLineSegment(sketch, "E87.MirrorCS", {"start": v(-30.05, -90) * mm, "end": v(-14.87, -108) * mm});
            skLineSegment(sketch, "E88.MirrorCS", {"start": v(-14.87, -108) * mm, "end": v(-15, -120) * mm});
            skArc(sketch, "E89.MirrorCS", {"start": v(14.98, -120.77) * mm, "mid": v(-0.39, -135) * mm, "end": v(-15, -120) * mm});
            skCircle(sketch, "E90.MirrorC", {"center": v(0, -120) * mm, "radius": 6 * mm});
            skLineSegment(sketch, "E91.MirrorCS", {"start": v(14.98, -108) * mm, "end": v(14.98, -120.77) * mm});
            skLineSegment(sketch, "E92.MirrorCS", {"start": v(32.98, -90) * mm, "end": v(14.98, -108) * mm});
            skLineSegment(sketch, "E93.MirrorCS", {"start": v(0, -90) * mm, "end": v(0, -120) * mm, "construction": true});
            skSolve(sketch);
        }
        {
            var Q0;
            Q0=makeQuery(id+"F16.imprint","IMPRINT",FACE,{"disambiguationData":[TD([[makeQuery(id+"F16.imprint","IMPRINT",EDGE,{"derivedFrom":sQuery(id+"F16.wireOp",EDGE,"E80")}),-1.0]])]});
            var Q1;
            Q1=makeQuery(id+"F16.imprint","IMPRINT",FACE,{"disambiguationData":[TD([[makeQuery(id+"F16.imprint","IMPRINT",EDGE,{"derivedFrom":makeQuery(id+"F1.opExtrude","CAP_EDGE",EDGE,{"disambiguationData":[OSD([sQuery(id+"F0.wireOp",EDGE,"E1.left")])],"isStart":true})}),-1.0]])]});
            var Q2;
            {var subQ0=sQuery(id+"F16.wireOp",EDGE,"E87.MirrorCS");Q2=makeQuery(id+"F16.imprint","IMPRINT",FACE,{"disambiguationData":[TD([[makeQuery(id+"F16.imprint","IMPRINT",EDGE,{"derivedFrom":subQ0}),1.0]])]});}
            var Q3;
            Q3=makeQuery(id+"F2.opExtrude","CAP_FACE",FACE,{"disambiguationData":[OSD([sQuery(id+"F0.wireOp",EDGE,"E12"),sQuery(id+"F0.wireOp",EDGE,"E13"),sQuery(id+"F0.wireOp",EDGE,"E14"),sQuery(id+"F0.wireOp",EDGE,"E15"),sQuery(id+"F0.wireOp",EDGE,"E17.filletArc"),sQuery(id+"F0.wireOp",EDGE,"E18.filletArc"),sQuery(id+"F0.wireOp",EDGE,"E19.filletArc"),sQuery(id+"F0.wireOp",EDGE,"E20.filletArc"),sQuery(id+"F0.wireOp",EDGE,"E25.0"),sQuery(id+"F0.wireOp",EDGE,"E25.1"),sQuery(id+"F0.wireOp",EDGE,"E25.2"),sQuery(id+"F0.wireOp",EDGE,"E25.3"),sQuery(id+"F0.wireOp",EDGE,"E25.4"),sQuery(id+"F0.wireOp",EDGE,"E25.5"),sQuery(id+"F0.wireOp",EDGE,"E25.6"),sQuery(id+"F0.wireOp",EDGE,"E25.7")])],"isStart":false});
            extrude(context, id + "F17", {"entities" : qUnion([Q0, Q1, Q2]), "endBound" : BoundingType.UP_TO_SURFACE, "depth" : 25 * mm, "endBoundEntityFace" : qUnion([Q3]), "offsetDistance" : 25 * mm});
        }
    });
